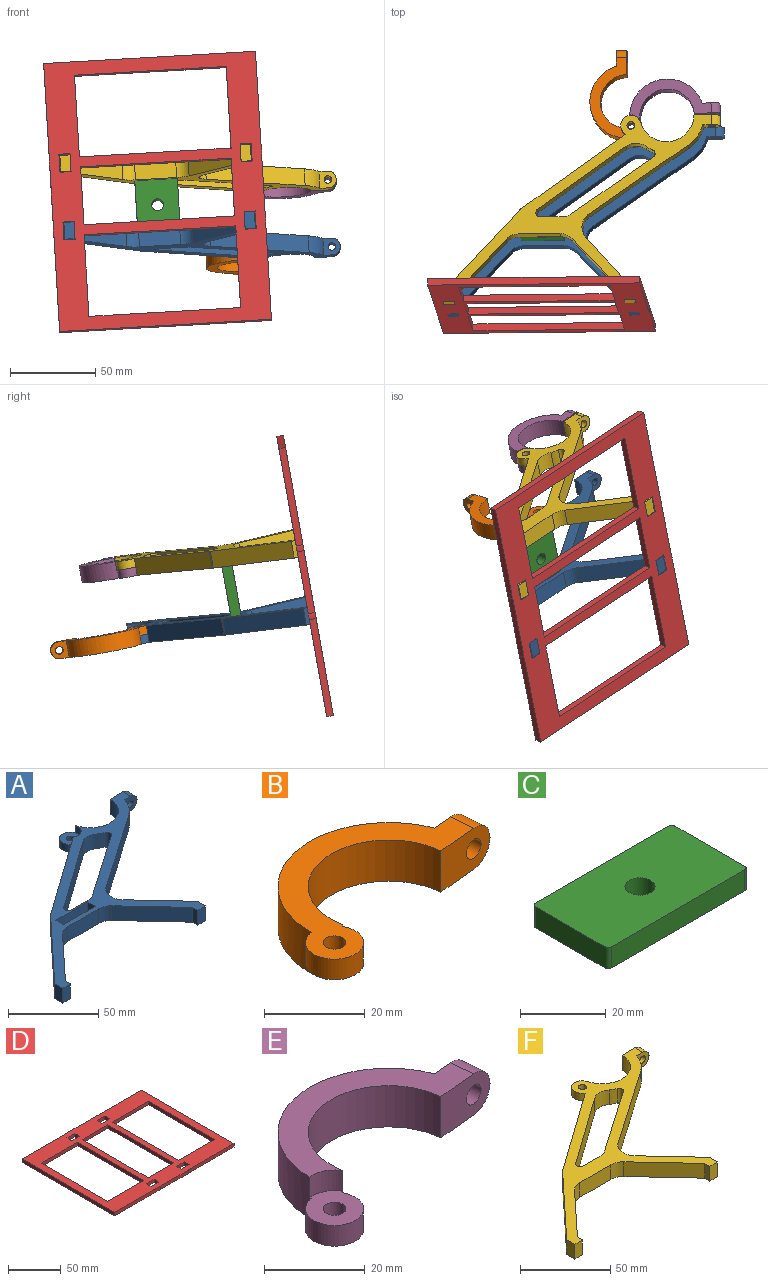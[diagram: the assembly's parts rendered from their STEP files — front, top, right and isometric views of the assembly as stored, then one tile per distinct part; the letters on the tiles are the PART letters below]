
ASSEMBLY  parts=6 mates=5
PART A: 42 faces, bbox 162.3x110x10 mm
  f0: cylinder r=6mm len=11.77mm, axis (0,0,-1), area 117.4mm2, adj f15,f16,f32,f41
  f1: cylinder r=2.25mm len=5mm, axis (0,0,-1), area 70.7mm2, adj f32,f41
  f2: plane 15.17x10mm, normal (0,1,0), area 125mm2, adj f15,f31,f32,f33,f34
  f3: plane 12.88x10mm, normal (0,1,0), area 128.8mm2, adj f4,f29,f31,f32
  f4: cylinder r=2.5mm len=10mm, axis (0,0,-1), area 63mm2, adj f3,f5,f31,f32
  f5: plane 51.81x36.97mm, normal (0.58,-0.81,0), area 636.4mm2, adj f4,f6,f31,f32
  f6: cylinder r=10mm len=11.46mm, axis (0,0,-1), area 122.1mm2, adj f5,f7,f31,f32
  f7: cylinder r=22.3mm len=10mm, axis (0,0,-1), area 47.4mm2, adj f6,f8,f31,f32
  f8: cylinder r=2.5mm len=10mm, axis (0,0,-1), area 53.7mm2, adj f7,f9,f31,f32
  f9: plane 47.87x33.21mm, normal (-0.57,0.82,0), area 582.6mm2, adj f8,f29,f31,f32
  f10: plane 30.19x28.13mm, normal (0.73,0.68,0), area 412.6mm2, adj f11,f30,f31,f32
  f11: cylinder r=10mm len=15.03mm, axis (0,0,-1), area 171.4mm2, adj f10,f12,f31,f32
  f12: plane 58.15x40.34mm, normal (0.57,-0.82,0), area 707.7mm2, adj f11,f13,f31,f32
  f13: cylinder r=22mm len=12.08mm, axis (0,0,-1), area 151.4mm2, adj f12,f14,f31,f32
  f14: plane 10x10mm, normal (0,-1,0), area 73.4mm2, adj f13,f31,f32,f33,f34
  f15: cylinder r=16mm len=31.39mm, axis (0,0,-1), area 458.5mm2, adj f0,f2,f31,f32,f40
  f16: plane 61.63x43.98mm, normal (-0.58,0.81,0), area 757.2mm2, adj f0,f17,f31,f32,f40
  f17: cylinder r=5mm len=10mm, axis (0,0,-1), area 10mm2, adj f16,f18,f31,f32
  f18: plane 47.8x44.54mm, normal (-0.73,0.68,0), area 653.4mm2, adj f17,f19,f31,f32
  f19: plane 10x6.36mm, normal (-1,0,0), area 63.6mm2, adj f18,f20,f31,f32
  f20: plane 10x6mm, normal (0,-1,0), area 60mm2, adj f19,f21,f31,f32
  f21: plane 10x4mm, normal (1,0,0), area 40mm2, adj f20,f22,f31,f32
  f22: plane 32.82x30.58mm, normal (0.73,-0.68,0), area 448.5mm2, adj f21,f23,f31,f32
  f23: cylinder r=10mm len=10mm, axis (0,0,-1), area 82.1mm2, adj f22,f24,f31,f32
  f24: plane 24.21x10mm, normal (0,-1,0), area 242.1mm2, adj f23,f25,f31,f32
  f25: cylinder r=10mm len=10mm, axis (0,0,-1), area 82.1mm2, adj f24,f26,f31,f32
  f26: plane 32.82x30.58mm, normal (-0.73,-0.68,0), area 448.5mm2, adj f25,f27,f31,f32
  f27: plane 10x4mm, normal (-1,0,0), area 40mm2, adj f26,f28,f31,f32
  f28: plane 10x6mm, normal (0,-1,0), area 60mm2, adj f27,f30,f31,f32
  f29: cylinder r=10mm len=10mm, axis (0,0,-1), area 60.7mm2, adj f3,f9,f31,f32
  f30: plane 10x6.36mm, normal (1,0,0), area 63.6mm2, adj f10,f28,f31,f32
  f31: plane 157.26x110mm, normal (0,0,1), area 2203.6mm2, adj f2,f3,f4,f5,f6,f7,f8,f9
  f32: plane 157.26x110mm, normal (0,0,-1), area 2450.8mm2, adj f0,f1,f2,f3,f4,f5,f6,f7
  f33: cylinder r=2.25mm len=6mm, axis (0,-1,0), area 84.8mm2, adj f2,f14
  f34: cylinder r=5mm len=10mm, axis (0,-1,0), area 94.2mm2, adj f2,f14,f31,f32
  f35: plane 8x6mm, normal (1,0,0), area 48mm2, adj f31,f36,f38,f39
  f36: plane 25x8mm, normal (0,1,0), area 200mm2, adj f31,f35,f37,f39
  f37: plane 8x6mm, normal (-1,0,0), area 48mm2, adj f31,f36,f38,f39
  f38: plane 25x8mm, normal (0,-1,0), area 200mm2, adj f31,f35,f37,f39
  f39: plane 25x6mm, normal (0,0,1), area 150mm2, adj f35,f36,f37,f38
  f40: cylinder r=6mm len=9mm, axis (0,0,1), area 71.1mm2, adj f15,f16,f31,f41
  f41: plane 12x12mm, normal (0,0,1), area 97.2mm2, adj f0,f1,f40
PART B: 13 faces, bbox 58x33.7x10 mm
  f0: plane 15.11x10mm, normal (0.09,-1,0), area 125mm2, adj f1,f5,f8,f11,f12
  f1: plane 53x33.69mm, normal (0,0,1), area 469mm2, adj f0,f2,f3,f4,f5,f6,f7,f12
  f2: plane 5x0.44mm, normal (0.49,-0.87,0), area 2.5mm2, adj f1,f3,f5,f10
  f3: cylinder r=5.75mm len=11.5mm, axis (0,0,-1), area 146.2mm2, adj f1,f2,f7,f10
  f4: cylinder r=2.25mm len=5mm, axis (0,0,-1), area 70.7mm2, adj f1,f10
  f5: cylinder r=16mm len=31.94mm, axis (0,0,-1), area 517.5mm2, adj f0,f1,f2,f8,f9
  f6: plane 10x9.96mm, normal (-0.09,1,0), area 73.4mm2, adj f1,f7,f8,f11,f12
  f7: cylinder r=22mm len=42.56mm, axis (0,0,-1), area 611.2mm2, adj f1,f3,f6,f8,f9,f10
  f8: plane 48.07x24.87mm, normal (0,0,-1), area 377.5mm2, adj f0,f5,f6,f7,f9,f12
  f9: cylinder r=6.25mm len=6.26mm, axis (0,0,-1), area 37.1mm2, adj f5,f7,f8,f10
  f10: plane 12x11.5mm, normal (0,0,-1), area 91.5mm2, adj f2,f3,f4,f7,f9
  f11: cylinder r=2.25mm len=6.37mm, axis (-0.09,1,0), area 84.8mm2, adj f0,f6
  f12: cylinder r=5mm len=10mm, axis (-0.09,1,0), area 94.2mm2, adj f0,f1,f6,f8
PART C: 11 faces, bbox 46x25x6 mm
  f0: plane 44x6mm, normal (0,1,0), area 264mm2, adj f5,f6,f7,f10
  f1: plane 23x6mm, normal (-1,0,0), area 138mm2, adj f5,f6,f7,f8
  f2: plane 44x6mm, normal (0,-1,0), area 264mm2, adj f5,f6,f8,f9
  f3: cylinder r=3.5mm len=7mm, axis (0,0,-1), area 131.9mm2, adj f5,f6
  f4: plane 23x6mm, normal (1,0,0), area 138mm2, adj f5,f6,f9,f10
  f5: plane 46x25mm, normal (0,0,1), area 1110.7mm2, adj f0,f1,f2,f3,f4,f7,f8,f9
  f6: plane 46x25mm, normal (0,0,-1), area 1110.7mm2, adj f0,f1,f2,f3,f4,f7,f8,f9
  f7: cylinder r=1mm len=6mm, axis (0,0,1), area 9.4mm2, adj f0,f1,f5,f6
  f8: cylinder r=1mm len=6mm, axis (0,0,-1), area 9.4mm2, adj f1,f2,f5,f6
  f9: cylinder r=1mm len=6mm, axis (0,0,1), area 9.4mm2, adj f2,f4,f5,f6
  f10: cylinder r=1mm len=6mm, axis (0,0,-1), area 9.4mm2, adj f0,f4,f5,f6
PART D: 42 faces, bbox 160x124.8x4 mm
  f0: plane 10.5x4mm, normal (0,1,0), area 42mm2, adj f1,f12,f13,f14
  f1: plane 6.5x4mm, normal (1,0,0), area 26mm2, adj f0,f2,f13,f14
  f2: plane 10.5x4mm, normal (0,-1,0), area 42mm2, adj f1,f12,f13,f14
  f3: cylinder r=9.17mm len=4mm, axis (0,0,-1), area 14.3mm2, adj f4,f11,f13,f14
  f4: plane 57.97x4mm, normal (0,1,0), area 231.9mm2, adj f3,f5,f13,f14
  f5: plane 124.5x4mm, normal (-1,0,0), area 498mm2, adj f4,f13,f14,f30
  f6: plane 89.16x4mm, normal (1,0,0), area 356.6mm2, adj f7,f13,f14,f31
  f7: plane 48.75x4mm, normal (0,-1,0), area 195mm2, adj f6,f8,f13,f14
  f8: plane 89.16x4mm, normal (-1,0,0), area 356.6mm2, adj f7,f13,f14,f31
  f9: plane 88.5x4mm, normal (1,0,0), area 354mm2, adj f10,f13,f14,f32
  f10: plane 34.5x4mm, normal (0,-1,0), area 138mm2, adj f9,f13,f14,f24
  f11: plane 36.94x4mm, normal (0,1,0), area 147.8mm2, adj f3,f13,f14,f18
  f12: plane 6.5x4mm, normal (-1,0,0), area 26mm2, adj f0,f2,f13,f14
  f13: plane 160x124.85mm, normal (0,0,1), area 7902.3mm2, adj f0,f1,f2,f3,f4,f5,f6,f7
  f14: plane 160x124.85mm, normal (0,0,-1), area 7902.3mm2, adj f0,f1,f2,f3,f4,f5,f6,f7
  f15: plane 10.5x4mm, normal (0,1,0), area 42mm2, adj f13,f14,f16,f25
  f16: plane 6.5x4mm, normal (-1,0,0), area 26mm2, adj f13,f14,f15,f17
  f17: plane 10.5x4mm, normal (0,-1,0), area 42mm2, adj f13,f14,f16,f25
  f18: cylinder r=9.17mm len=4mm, axis (0,0,-1), area 14.3mm2, adj f11,f13,f14,f19
  f19: plane 57.97x4mm, normal (0,1,0), area 231.9mm2, adj f13,f14,f18,f20
  f20: plane 124.5x4mm, normal (1,0,0), area 498mm2, adj f13,f14,f19,f39
  f21: plane 89.16x4mm, normal (-1,0,0), area 356.6mm2, adj f13,f14,f22,f40
  f22: plane 48.75x4mm, normal (0,-1,0), area 195mm2, adj f13,f14,f21,f23
  f23: plane 89.16x4mm, normal (1,0,0), area 356.6mm2, adj f13,f14,f22,f40
  f24: plane 88.5x4mm, normal (-1,0,0), area 354mm2, adj f10,f13,f14,f32
  f25: plane 6.5x4mm, normal (1,0,0), area 26mm2, adj f13,f14,f15,f17
  f26: plane 10.5x4mm, normal (0,-1,0), area 42mm2, adj f13,f14,f27,f34
  f27: plane 6.5x4mm, normal (1,0,0), area 26mm2, adj f13,f14,f26,f28
  f28: plane 10.5x4mm, normal (0,1,0), area 42mm2, adj f13,f14,f27,f34
  f29: cylinder r=9.17mm len=4mm, axis (0,0,-1), area 14.3mm2, adj f13,f14,f30,f33
  f30: plane 57.97x4mm, normal (0,-1,0), area 231.9mm2, adj f5,f13,f14,f29
  f31: plane 48.75x4mm, normal (0,1,0), area 195mm2, adj f6,f8,f13,f14
  f32: plane 34.5x4mm, normal (0,1,0), area 138mm2, adj f9,f13,f14,f24
  f33: plane 36.94x4mm, normal (0,-1,0), area 147.8mm2, adj f13,f14,f29,f38
  f34: plane 6.5x4mm, normal (-1,0,0), area 26mm2, adj f13,f14,f26,f28
  f35: plane 10.5x4mm, normal (0,-1,0), area 42mm2, adj f13,f14,f36,f41
  f36: plane 6.5x4mm, normal (-1,0,0), area 26mm2, adj f13,f14,f35,f37
  f37: plane 10.5x4mm, normal (0,1,0), area 42mm2, adj f13,f14,f36,f41
  f38: cylinder r=9.17mm len=4mm, axis (0,0,-1), area 14.3mm2, adj f13,f14,f33,f39
  f39: plane 57.97x4mm, normal (0,-1,0), area 231.9mm2, adj f13,f14,f20,f38
  f40: plane 48.75x4mm, normal (0,1,0), area 195mm2, adj f13,f14,f21,f23
  f41: plane 6.5x4mm, normal (1,0,0), area 26mm2, adj f13,f14,f35,f37
PART E: 13 faces, bbox 58x33.7x10 mm
  f0: plane 15.11x10mm, normal (0.09,-1,0), area 125mm2, adj f1,f5,f8,f11,f12
  f1: plane 53x33.69mm, normal (0,0,-1), area 469mm2, adj f0,f2,f3,f4,f5,f6,f7,f12
  f2: plane 5x0.44mm, normal (0.49,-0.87,0), area 2.5mm2, adj f1,f3,f5,f10
  f3: cylinder r=5.75mm len=11.5mm, axis (0,0,1), area 146.2mm2, adj f1,f2,f7,f10
  f4: cylinder r=2.25mm len=5mm, axis (0,0,1), area 70.7mm2, adj f1,f10
  f5: cylinder r=16mm len=31.94mm, axis (0,0,1), area 517.5mm2, adj f0,f1,f2,f8,f9
  f6: plane 10x9.96mm, normal (-0.09,1,0), area 73.4mm2, adj f1,f7,f8,f11,f12
  f7: cylinder r=22mm len=42.56mm, axis (0,0,1), area 611.2mm2, adj f1,f3,f6,f8,f9,f10
  f8: plane 48.07x24.87mm, normal (0,0,1), area 377.5mm2, adj f0,f5,f6,f7,f9,f12
  f9: cylinder r=6.25mm len=6.26mm, axis (0,0,1), area 37.1mm2, adj f5,f7,f8,f10
  f10: plane 12x11.5mm, normal (0,0,1), area 91.5mm2, adj f2,f3,f4,f7,f9
  f11: cylinder r=2.25mm len=6.37mm, axis (-0.09,1,0), area 84.8mm2, adj f0,f6
  f12: cylinder r=5mm len=10mm, axis (-0.09,1,0), area 94.2mm2, adj f0,f1,f6,f8
PART F: 42 faces, bbox 162.3x110x10 mm
  f0: cylinder r=6mm len=11.77mm, axis (0,0,1), area 117.4mm2, adj f15,f16,f32,f41
  f1: cylinder r=2.25mm len=5mm, axis (0,0,1), area 70.7mm2, adj f32,f41
  f2: plane 15.17x10mm, normal (0,1,0), area 125mm2, adj f15,f31,f32,f33,f34
  f3: plane 12.88x10mm, normal (0,1,0), area 128.8mm2, adj f4,f29,f31,f32
  f4: cylinder r=2.5mm len=10mm, axis (0,0,1), area 63mm2, adj f3,f5,f31,f32
  f5: plane 51.81x36.97mm, normal (0.58,-0.81,0), area 636.4mm2, adj f4,f6,f31,f32
  f6: cylinder r=10mm len=11.46mm, axis (0,0,1), area 122.1mm2, adj f5,f7,f31,f32
  f7: cylinder r=22.3mm len=10mm, axis (0,0,1), area 47.4mm2, adj f6,f8,f31,f32
  f8: cylinder r=2.5mm len=10mm, axis (0,0,1), area 53.7mm2, adj f7,f9,f31,f32
  f9: plane 47.87x33.21mm, normal (-0.57,0.82,0), area 582.6mm2, adj f8,f29,f31,f32
  f10: plane 30.19x28.13mm, normal (0.73,0.68,0), area 412.6mm2, adj f11,f30,f31,f32
  f11: cylinder r=10mm len=15.03mm, axis (0,0,1), area 171.4mm2, adj f10,f12,f31,f32
  f12: plane 58.15x40.34mm, normal (0.57,-0.82,0), area 707.7mm2, adj f11,f13,f31,f32
  f13: cylinder r=22mm len=12.08mm, axis (0,0,1), area 151.4mm2, adj f12,f14,f31,f32
  f14: plane 10x10mm, normal (0,-1,0), area 73.4mm2, adj f13,f31,f32,f33,f34
  f15: cylinder r=16mm len=31.39mm, axis (0,0,1), area 458.5mm2, adj f0,f2,f31,f32,f40
  f16: plane 61.63x43.98mm, normal (-0.58,0.81,0), area 757.2mm2, adj f0,f17,f31,f32,f40
  f17: cylinder r=5mm len=10mm, axis (0,0,1), area 10mm2, adj f16,f18,f31,f32
  f18: plane 47.8x44.54mm, normal (-0.73,0.68,0), area 653.4mm2, adj f17,f19,f31,f32
  f19: plane 10x6.36mm, normal (-1,0,0), area 63.6mm2, adj f18,f20,f31,f32
  f20: plane 10x6mm, normal (0,-1,0), area 60mm2, adj f19,f21,f31,f32
  f21: plane 10x4mm, normal (1,0,0), area 40mm2, adj f20,f22,f31,f32
  f22: plane 32.82x30.58mm, normal (0.73,-0.68,0), area 448.5mm2, adj f21,f23,f31,f32
  f23: cylinder r=10mm len=10mm, axis (0,0,1), area 82.1mm2, adj f22,f24,f31,f32
  f24: plane 24.21x10mm, normal (0,-1,0), area 242.1mm2, adj f23,f25,f31,f32
  f25: cylinder r=10mm len=10mm, axis (0,0,1), area 82.1mm2, adj f24,f26,f31,f32
  f26: plane 32.82x30.58mm, normal (-0.73,-0.68,0), area 448.5mm2, adj f25,f27,f31,f32
  f27: plane 10x4mm, normal (-1,0,0), area 40mm2, adj f26,f28,f31,f32
  f28: plane 10x6mm, normal (0,-1,0), area 60mm2, adj f27,f30,f31,f32
  f29: cylinder r=10mm len=10mm, axis (0,0,1), area 60.7mm2, adj f3,f9,f31,f32
  f30: plane 10x6.36mm, normal (1,0,0), area 63.6mm2, adj f10,f28,f31,f32
  f31: plane 157.26x110mm, normal (0,0,-1), area 2203.6mm2, adj f2,f3,f4,f5,f6,f7,f8,f9
  f32: plane 157.26x110mm, normal (0,0,1), area 2450.8mm2, adj f0,f1,f2,f3,f4,f5,f6,f7
  f33: cylinder r=2.25mm len=6mm, axis (0,-1,0), area 84.8mm2, adj f2,f14
  f34: cylinder r=5mm len=10mm, axis (0,-1,0), area 94.2mm2, adj f2,f14,f31,f32
  f35: plane 8x6mm, normal (1,0,0), area 48mm2, adj f31,f36,f38,f39
  f36: plane 25x8mm, normal (0,1,0), area 200mm2, adj f31,f35,f37,f39
  f37: plane 8x6mm, normal (-1,0,0), area 48mm2, adj f31,f36,f38,f39
  f38: plane 25x8mm, normal (0,-1,0), area 200mm2, adj f31,f35,f37,f39
  f39: plane 25x6mm, normal (0,0,-1), area 150mm2, adj f35,f36,f37,f38
  f40: cylinder r=6mm len=9mm, axis (0,0,-1), area 71.1mm2, adj f15,f16,f31,f41
  f41: plane 12x12mm, normal (0,0,-1), area 97.2mm2, adj f0,f1,f40
PLACE A rot(axis=(-0.95,-0.31,0.03),10.7deg) t=(-40.46,-35.67,-26.24)mm
PLACE B rot(axis=(-0.12,0.06,0.99),86.8deg) t=(184.97,-47.55,-10.63)mm
PLACE C rot(axis=(-0.59,-0.62,-0.52),127.7deg) t=(14.26,13.7,-11.43)mm fixed
PLACE D rot(axis=(-0.59,-0.62,-0.52),127.7deg) t=(14.25,-29.57,-3.45)mm
PLACE E rot(axis=(-0.94,-0.33,-0.1),10.7deg) t=(-39.99,-63.19,-82.35)mm
PLACE F rot(axis=(-0.95,-0.31,0.03),10.7deg) t=(-36.94,-46.2,-85.2)mm
MATE revolute B.f3 <-> A.f0  axis (0.06,-0.18,-0.98) through (69.27,67.85,-38.16)mm
MATE revolute F.f0 <-> E.f3  axis (-0.06,0.18,0.98) through (66.92,74.87,1.15)mm
MATE fastened F.f39 <-> C.f4  axis (0.06,-0.18,-0.98) through (12.91,17.74,11.17)mm
MATE fastened A.f39 <-> C.f1  axis (-0.06,0.18,0.98) through (15.62,9.67,-34.03)mm
MATE fastened A.f21 <-> D.f26  axis (1,0.01,0.06) through (-34.47,-33.64,-26.24)mm
